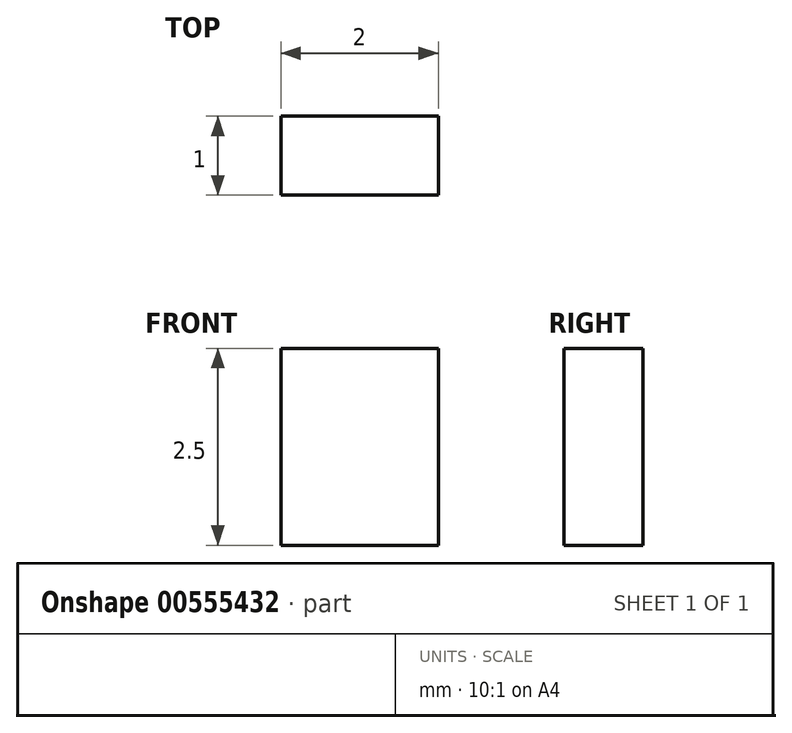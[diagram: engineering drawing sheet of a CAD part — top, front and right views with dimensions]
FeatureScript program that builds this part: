
annotation { "Feature Type Name" : "Feature", "Feature Type Description" : "" }
export const myFeature = defineFeature(function(context is Context, id is Id, definition is map)
    precondition{}
    {
        {
            var Q0;
            Q0=qCreatedBy(makeId("Front.planeOp"),FACE);
            var sketch = newSketch(context, id + "F0", { "sketchPlane" : qUnion([Q0])});
            skLineSegment(sketch, "E0.bottom", {"start": v(-1, 1.25) * mm, "end": v(1, 1.25) * mm});
            skLineSegment(sketch, "E0.top", {"start": v(-1, -1.25) * mm, "end": v(1, -1.25) * mm});
            skLineSegment(sketch, "E0.left", {"start": v(-1, 1.25) * mm, "end": v(-1, -1.25) * mm});
            skLineSegment(sketch, "E0.right", {"start": v(1, 1.25) * mm, "end": v(1, -1.25) * mm});
            skPoint(sketch, "E0.middle", {"position": v(0, 0) * mm});
            skSolve(sketch);
        }
        {
            var Q0;
            Q0 = qSketchRegion(id + "F0", true);
            extrude(context, id + "F1", {"entities" : qUnion([Q0]), "depth" : 1 * mm, "offsetDistance" : 25.4 * mm});
        }
    });
